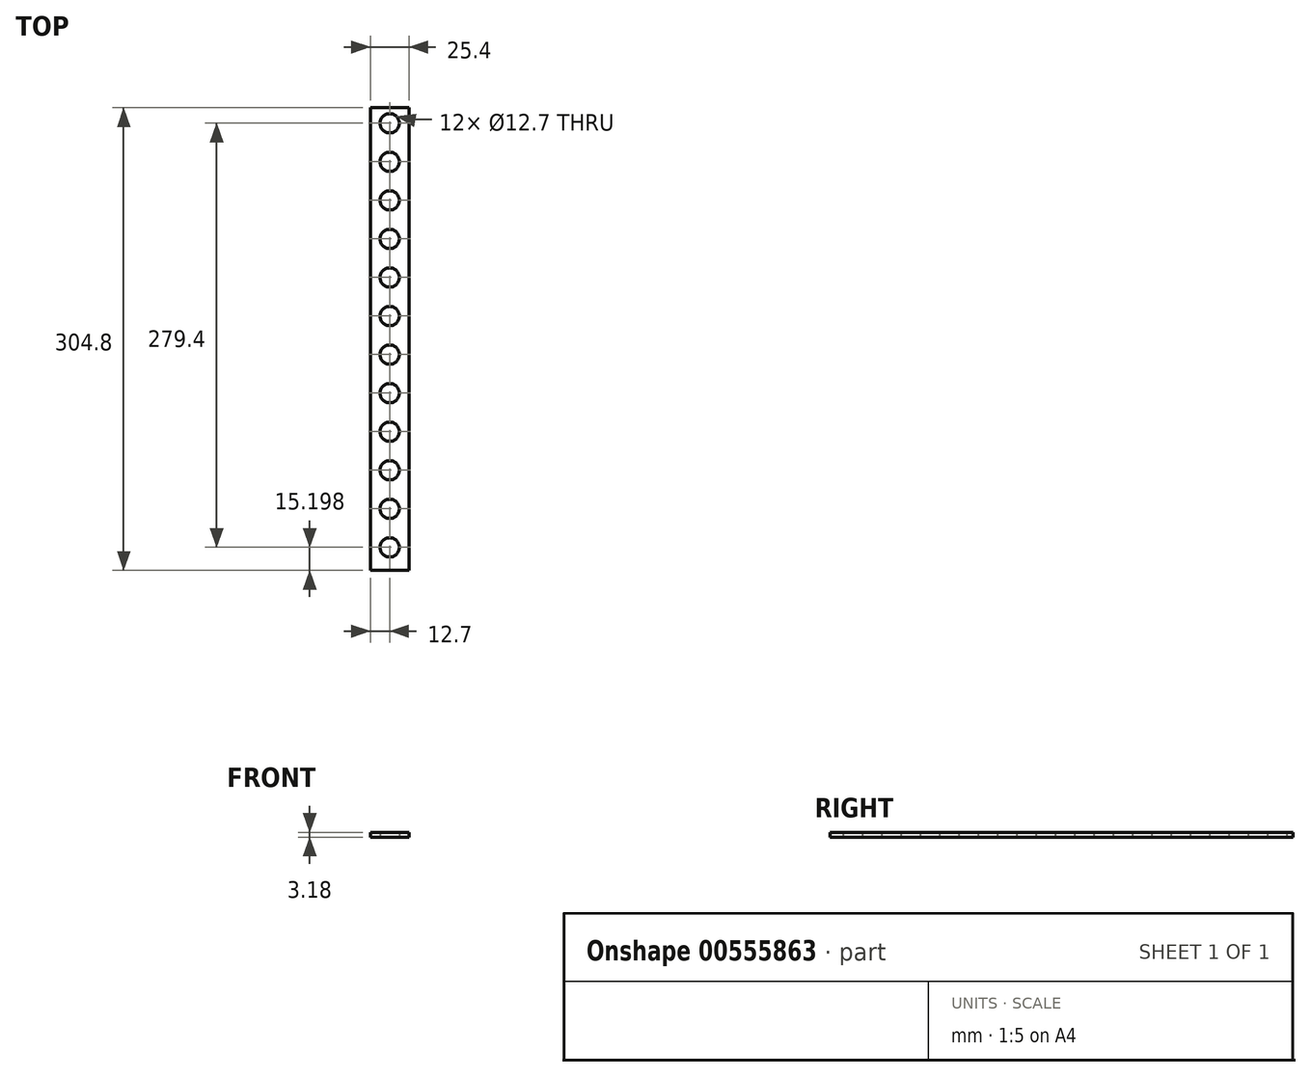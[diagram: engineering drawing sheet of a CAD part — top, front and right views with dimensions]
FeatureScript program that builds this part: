
annotation { "Feature Type Name" : "Feature", "Feature Type Description" : "" }
export const myFeature = defineFeature(function(context is Context, id is Id, definition is map)
    precondition{}
    {
        {
            var Q0;
            Q0=qCreatedBy(makeId("Top.planeOp"),FACE);
            var sketch = newSketch(context, id + "F0", { "sketchPlane" : qUnion([Q0])});
            skLineSegment(sketch, "E0.bottom", {"start": v(-12.7, -152.4) * mm, "end": v(12.7, -152.4) * mm});
            skLineSegment(sketch, "E0.top", {"start": v(-12.7, 152.4) * mm, "end": v(12.7, 152.4) * mm});
            skLineSegment(sketch, "E0.left", {"start": v(-12.7, -152.4) * mm, "end": v(-12.7, 152.4) * mm});
            skLineSegment(sketch, "E0.right", {"start": v(12.7, -152.4) * mm, "end": v(12.7, 152.4) * mm});
            skPoint(sketch, "E0.middle", {"position": v(0, 0) * mm});
            skSolve(sketch);
        }
        {
            var Q0;
            Q0=makeQuery(id+"F0.imprint","IMPRINT",FACE,{"disambiguationData":[TD([[makeQuery(id+"F0.imprint","IMPRINT",EDGE,{"derivedFrom":sQuery(id+"F0.wireOp",EDGE,"E0.bottom")}),1.0]])]});
            extrude(context, id + "F1", {"entities" : qUnion([Q0]), "depth" : 3.17 * mm, "offsetDistance" : 25.4 * mm});
        }
        {
            var Q0;
            Q0=qCreatedBy(makeId("Top.planeOp"),FACE);
            var sketch = newSketch(context, id + "F2", { "sketchPlane" : qUnion([Q0])});
            skCircle(sketch, "E1", {"center": v(0, -137.2) * mm, "radius": 6.35 * mm});
            skCircle(sketch, "E2.0.1.0", {"center": v(0, -111.8) * mm, "radius": 6.35 * mm});
            skLineSegment(sketch, "E2.direction2", {"start": v(0, -137.2) * mm, "end": v(0, -111.8) * mm, "construction": true});
            skCircle(sketch, "E3.0.1.0", {"center": v(0, -86.4) * mm, "radius": 6.35 * mm});
            skLineSegment(sketch, "E3.direction2", {"start": v(0, -111.8) * mm, "end": v(0, -86.4) * mm, "construction": true});
            skCircle(sketch, "E4.0.1.0", {"center": v(0, -61) * mm, "radius": 6.35 * mm});
            skCircle(sketch, "E4.0.1.1", {"center": v(0, -35.6) * mm, "radius": 6.35 * mm});
            skLineSegment(sketch, "E4.0.1.2", {"start": v(0, -61) * mm, "end": v(0, -35.6) * mm, "construction": true});
            skLineSegment(sketch, "E4.0.1.3", {"start": v(0, -35.6) * mm, "end": v(0, -10.2) * mm, "construction": true});
            skCircle(sketch, "E4.0.1.4", {"center": v(0, -10.2) * mm, "radius": 6.35 * mm});
            skLineSegment(sketch, "E4.direction2", {"start": v(0, -137.2) * mm, "end": v(0, -61) * mm, "construction": true});
            skCircle(sketch, "E5.0.1.0", {"center": v(0, 116.8) * mm, "radius": 6.35 * mm});
            skCircle(sketch, "E5.0.1.1", {"center": v(0, 91.4) * mm, "radius": 6.35 * mm});
            skLineSegment(sketch, "E5.0.1.2", {"start": v(0, 40.6) * mm, "end": v(0, 66) * mm, "construction": true});
            skCircle(sketch, "E5.0.1.3", {"center": v(0, 66) * mm, "radius": 6.35 * mm});
            skLineSegment(sketch, "E5.0.1.4", {"start": v(0, 15.2) * mm, "end": v(0, 40.6) * mm, "construction": true});
            skCircle(sketch, "E5.0.1.5", {"center": v(0, 40.6) * mm, "radius": 6.35 * mm});
            skCircle(sketch, "E5.0.1.6", {"center": v(0, 15.2) * mm, "radius": 6.35 * mm});
            skLineSegment(sketch, "E5.0.1.7", {"start": v(0, 15.2) * mm, "end": v(0, 91.4) * mm, "construction": true});
            skCircle(sketch, "E5.0.1.8", {"center": v(0, 142.2) * mm, "radius": 6.35 * mm});
            skLineSegment(sketch, "E5.0.1.9", {"start": v(0, 116.8) * mm, "end": v(0, 142.2) * mm, "construction": true});
            skLineSegment(sketch, "E5.0.1.10", {"start": v(0, 91.4) * mm, "end": v(0, 116.8) * mm, "construction": true});
            skLineSegment(sketch, "E5.direction2", {"start": v(0, -137.2) * mm, "end": v(0, 15.2) * mm, "construction": true});
            skSolve(sketch);
        }
        {
            var Q0;
            Q0=sQuery(id+"F2.wireOp",VERTEX,"E5.direction2.start");
            var Q1;
            Q1=makeQuery(id+"F1.opExtrude","SWEPT_BODY",BODY,{"disambiguationData":[OSD([sQuery(id+"F0.wireOp",EDGE,"E0.bottom"),sQuery(id+"F0.wireOp",EDGE,"E0.top"),sQuery(id+"F0.wireOp",EDGE,"E0.left"),sQuery(id+"F0.wireOp",EDGE,"E0.right")])]});
            hole(context, id + "F3", {"style" : HoleStyle.SIMPLE, "endStyle" : HoleEndStyle.BLIND, "oppositeDirection" : true, "holeDiameter" : 12.7 * mm, "holeDepth" : 25.4 * mm, "isTappedThrough" : true, "tappedDepth" : 12.7 * mm, "tapClearance" : 3, "startFromSketch" : true, "locations" : qUnion([Q0]), "scope" : qUnion([Q1])});
        }
        {
            var Q0;
            Q0=sQuery(id+"F2.wireOp",VERTEX,"E3.direction2.start");
            var Q1;
            Q1=makeQuery(id+"F1.opExtrude","SWEPT_BODY",BODY,{"disambiguationData":[OSD([sQuery(id+"F0.wireOp",EDGE,"E0.bottom"),sQuery(id+"F0.wireOp",EDGE,"E0.top"),sQuery(id+"F0.wireOp",EDGE,"E0.left"),sQuery(id+"F0.wireOp",EDGE,"E0.right")])]});
            hole(context, id + "F4", {"style" : HoleStyle.SIMPLE, "endStyle" : HoleEndStyle.BLIND, "oppositeDirection" : true, "holeDiameter" : 12.7 * mm, "holeDepth" : 25.4 * mm, "isTappedThrough" : true, "tappedDepth" : 12.7 * mm, "tapClearance" : 3, "startFromSketch" : true, "locations" : qUnion([Q0]), "scope" : qUnion([Q1])});
        }
        {
            var Q0;
            Q0=sQuery(id+"F2.wireOp",VERTEX,"E3.direction2.end");
            var Q1;
            Q1=makeQuery(id+"F1.opExtrude","SWEPT_BODY",BODY,{"disambiguationData":[OSD([sQuery(id+"F0.wireOp",EDGE,"E0.bottom"),sQuery(id+"F0.wireOp",EDGE,"E0.top"),sQuery(id+"F0.wireOp",EDGE,"E0.left"),sQuery(id+"F0.wireOp",EDGE,"E0.right")])]});
            hole(context, id + "F5", {"style" : HoleStyle.SIMPLE, "endStyle" : HoleEndStyle.BLIND, "oppositeDirection" : true, "holeDiameter" : 12.7 * mm, "holeDepth" : 25.4 * mm, "isTappedThrough" : true, "tappedDepth" : 12.7 * mm, "tapClearance" : 3, "startFromSketch" : true, "locations" : qUnion([Q0]), "scope" : qUnion([Q1]), "majorDiameter" : 6.35 * mm});
        }
        {
            var Q0;
            Q0=sQuery(id+"F2.wireOp",VERTEX,"E4.0.1.0.center");
            var Q1;
            Q1=makeQuery(id+"F1.opExtrude","SWEPT_BODY",BODY,{"disambiguationData":[OSD([sQuery(id+"F0.wireOp",EDGE,"E0.bottom"),sQuery(id+"F0.wireOp",EDGE,"E0.top"),sQuery(id+"F0.wireOp",EDGE,"E0.left"),sQuery(id+"F0.wireOp",EDGE,"E0.right")])]});
            hole(context, id + "F6", {"style" : HoleStyle.SIMPLE, "endStyle" : HoleEndStyle.BLIND, "oppositeDirection" : true, "holeDiameter" : 12.7 * mm, "holeDepth" : 25.4 * mm, "isTappedThrough" : true, "tappedDepth" : 12.7 * mm, "tapClearance" : 3, "startFromSketch" : true, "locations" : qUnion([Q0]), "scope" : qUnion([Q1])});
        }
        {
            var Q0;
            Q0=sQuery(id+"F2.wireOp",VERTEX,"E4.0.1.1.center");
            var Q1;
            Q1=sQuery(id+"F2.wireOp",VERTEX,"E4.0.1.3.end");
            var Q2;
            Q2=sQuery(id+"F2.wireOp",VERTEX,"E5.0.1.4.start");
            var Q3;
            Q3=sQuery(id+"F2.wireOp",VERTEX,"E5.0.1.2.start");
            var Q4;
            Q4=sQuery(id+"F2.wireOp",VERTEX,"E5.0.1.2.end");
            var Q5;
            Q5=sQuery(id+"F2.wireOp",VERTEX,"E5.0.1.1.center");
            var Q6;
            Q6=sQuery(id+"F2.wireOp",VERTEX,"E5.0.1.9.start");
            var Q7;
            Q7=sQuery(id+"F2.wireOp",VERTEX,"E5.0.1.8.center");
            var Q8;
            Q8=makeQuery(id+"F1.opExtrude","SWEPT_BODY",BODY,{"disambiguationData":[OSD([sQuery(id+"F0.wireOp",EDGE,"E0.bottom"),sQuery(id+"F0.wireOp",EDGE,"E0.top"),sQuery(id+"F0.wireOp",EDGE,"E0.left"),sQuery(id+"F0.wireOp",EDGE,"E0.right")])]});
            hole(context, id + "F7", {"style" : HoleStyle.SIMPLE, "endStyle" : HoleEndStyle.BLIND, "oppositeDirection" : true, "holeDiameter" : 12.7 * mm, "holeDepth" : 25.4 * mm, "isTappedThrough" : true, "tappedDepth" : 12.7 * mm, "tapClearance" : 3, "startFromSketch" : true, "locations" : qUnion([Q0, Q1, Q2, Q3, Q4, Q5, Q6, Q7]), "scope" : qUnion([Q8])});
        }
    });
